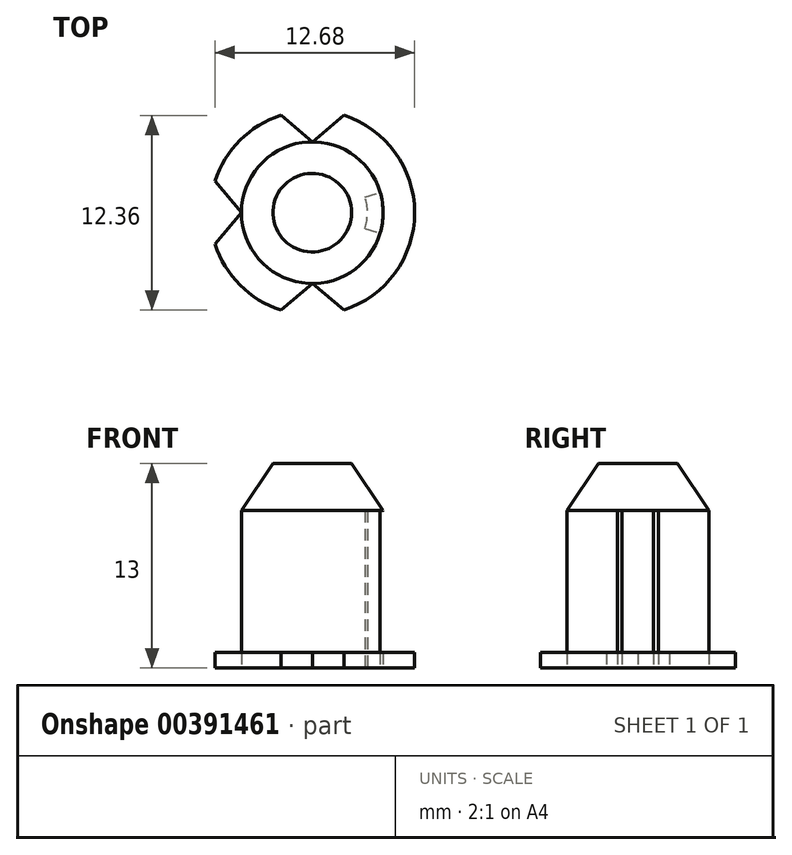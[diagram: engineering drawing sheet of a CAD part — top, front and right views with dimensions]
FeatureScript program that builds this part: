
annotation { "Feature Type Name" : "Feature", "Feature Type Description" : "" }
export const myFeature = defineFeature(function(context is Context, id is Id, definition is map)
    precondition{}
    {
        {
            var Q0;
            Q0=qCreatedBy(makeId("Top.planeOp"),FACE);
            var sketch = newSketch(context, id + "F0", { "sketchPlane" : qUnion([Q0])});
            skCircle(sketch, "E0", {"center": v(0, 0) * mm, "radius": 1.25 * mm});
            skCircle(sketch, "E1", {"center": v(0, 0) * mm, "radius": 6.5 * mm});
            skCircle(sketch, "E2.0", {"center": v(0, 0) * mm, "radius": 4.5 * mm});
            skArc(sketch, "E3", {"start": v(-6.18, 2) * mm, "mid": v(-6.5, 0) * mm, "end": v(-6.18, -2) * mm});
            skPoint(sketch, "E4.endSnap0", {"position": v(-6.5, 0) * mm});
            skCircle(sketch, "E5.0", {"center": v(0, 0) * mm, "radius": 3.5 * mm});
            skArc(sketch, "E6", {"start": v(3.35, -1) * mm, "mid": v(3.5, 0) * mm, "end": v(3.35, 1) * mm});
            skArc(sketch, "E7.0", {"start": v(4.3, -1.3) * mm, "mid": v(4.5, 0) * mm, "end": v(4.3, 1.3) * mm});
            skLineSegment(sketch, "E8", {"start": v(3.35, 1) * mm, "end": v(4.3, 1.3) * mm});
            skLineSegment(sketch, "E9", {"start": v(3.35, -1) * mm, "end": v(4.3, -1.3) * mm});
            skLineSegment(sketch, "E10", {"start": v(-6.18, 2) * mm, "end": v(-4.5, 0) * mm});
            skLineSegment(sketch, "E11", {"start": v(-4.5, 0) * mm, "end": v(-6.18, -2) * mm});
            skLineSegment(sketch, "E12", {"start": v(3.5, 0) * mm, "end": v(3.35, 1) * mm, "construction": true});
            skLineSegment(sketch, "E13", {"start": v(3.5, 0) * mm, "end": v(3.35, -1) * mm, "construction": true});
            skLineSegment(sketch, "E14", {"start": v(-4.5, 0) * mm, "end": v(-3.5, 0) * mm, "construction": true});
            skArc(sketch, "E15", {"start": v(-2, -6.18) * mm, "mid": v(0, -6.5) * mm, "end": v(2, -6.18) * mm});
            skLineSegment(sketch, "E16", {"start": v(-2, -6.18) * mm, "end": v(0, -4.5) * mm});
            skLineSegment(sketch, "E17", {"start": v(0, -4.5) * mm, "end": v(2, -6.18) * mm});
            skArc(sketch, "E18", {"start": v(2, 6.18) * mm, "mid": v(0, 6.5) * mm, "end": v(-2, 6.18) * mm});
            skLineSegment(sketch, "E19", {"start": v(2, 6.18) * mm, "end": v(0, 4.5) * mm});
            skLineSegment(sketch, "E20", {"start": v(0, 4.5) * mm, "end": v(-2, 6.18) * mm});
            skLineSegment(sketch, "E21", {"start": v(-3.5, 0) * mm, "end": v(-1.25, 0) * mm, "construction": true});
            skLineSegment(sketch, "E22", {"start": v(-1.25, 0) * mm, "end": v(1.25, 0) * mm, "construction": true});
            skLineSegment(sketch, "E23", {"start": v(1.25, 0) * mm, "end": v(3.5, 0) * mm, "construction": true});
            skLineSegment(sketch, "E24", {"start": v(3.35, -1) * mm, "end": v(1.2, -0.32) * mm, "construction": true});
            skLineSegment(sketch, "E25", {"start": v(3.35, 1) * mm, "end": v(1.2, 0.32) * mm, "construction": true});
            skCircle(sketch, "E26", {"center": v(0, 0) * mm, "radius": 2.5 * mm});
            skSolve(sketch);
        }
        {
            var Q0;
            {var subQ4=sQuery(id+"F0.wireOp",EDGE,"E10");Q0=makeQuery(id+"F0.imprint","IMPRINT",FACE,{"disambiguationData":[TD([[makeQuery(id+"F0.imprint","IMPRINT",EDGE,{"derivedFrom":subQ4}),1.0]])]});}
            var Q1;
            {var subQ0=sQuery(id+"F0.wireOp",EDGE,"E8");Q1=makeQuery(id+"F0.imprint","IMPRINT",FACE,{"disambiguationData":[TD([[makeQuery(id+"F0.imprint","IMPRINT",EDGE,{"derivedFrom":subQ0}),1.0]])]});}
            var Q2;
            {var subQ0=sQuery(id+"F0.wireOp",EDGE,"E11");Q2=makeQuery(id+"F0.imprint","IMPRINT",FACE,{"disambiguationData":[TD([[makeQuery(id+"F0.imprint","IMPRINT",EDGE,{"derivedFrom":subQ0}),1.0]])]});}
            var Q3;
            {var subQ2=sQuery(id+"F0.wireOp",EDGE,"E17");Q3=makeQuery(id+"F0.imprint","IMPRINT",FACE,{"disambiguationData":[TD([[makeQuery(id+"F0.imprint","IMPRINT",EDGE,{"derivedFrom":subQ2}),1.0]])]});}
            extrude(context, id + "F1", {"entities" : qUnion([Q0, Q1, Q2, Q3]), "depth" : 1 * mm});
        }
        {
            var Q0;
            {var subQ5=sQuery(id+"F0.wireOp",EDGE,"E8");Q0=makeQuery(id+"F0.imprint","IMPRINT",FACE,{"disambiguationData":[TD([[makeQuery(id+"F0.imprint","IMPRINT",EDGE,{"derivedFrom":subQ5}),1.0]])]});}
            var Q1;
            Q1=makeQuery(id+"F0.imprint","IMPRINT",FACE,{"disambiguationData":[TD([[makeQuery(id+"F0.imprint","IMPRINT",EDGE,{"derivedFrom":sQuery(id+"F0.wireOp",EDGE,"E26")}),-1.0]])]});
            var Q2;
            Q2=makeQuery(id+"F0.imprint","IMPRINT",FACE,{"disambiguationData":[TD([[makeQuery(id+"F0.imprint","IMPRINT",EDGE,{"derivedFrom":sQuery(id+"F0.wireOp",EDGE,"E0")}),-1.0]])]});
            var Q3;
            Q3=makeQuery(id+"F0.imprint","IMPRINT",FACE,{"disambiguationData":[TD([[makeQuery(id+"F0.imprint","IMPRINT",EDGE,{"derivedFrom":sQuery(id+"F0.wireOp",EDGE,"E0")}),1.0]])]});
            var Q4;
            {var subQ0=sQuery(id+"F0.wireOp",EDGE,"E8");Q4=makeQuery(id+"F0.imprint","IMPRINT",FACE,{"disambiguationData":[TD([[makeQuery(id+"F0.imprint","IMPRINT",EDGE,{"derivedFrom":subQ0}),-1.0]])]});}
            extrude(context, id + "F2", {"entities" : qUnion([Q0, Q1, Q2, Q3, Q4]), "operationType" : NewBodyOperationType.ADD, "depth" : 10 * mm});
        }
        {
            var Q0;
            Q0=makeQuery(id+"F1.opExtrude","SWEPT_BODY",BODY,{"disambiguationData":[OSD([sQuery(id+"F0.wireOp",EDGE,"E1"),sQuery(id+"F0.wireOp",EDGE,"E2.0"),sQuery(id+"F0.wireOp",EDGE,"E5.0"),sQuery(id+"F0.wireOp",EDGE,"E8"),sQuery(id+"F0.wireOp",EDGE,"E9"),sQuery(id+"F0.wireOp",EDGE,"E10"),sQuery(id+"F0.wireOp",EDGE,"E11"),sQuery(id+"F0.wireOp",EDGE,"E16"),sQuery(id+"F0.wireOp",EDGE,"E17"),sQuery(id+"F0.wireOp",EDGE,"E19"),sQuery(id+"F0.wireOp",EDGE,"E20")])]});
            transform(context, id + "F3", {"entities" : qUnion([Q0]), "transformType" : TransformType.TRANSLATION_3D, "dx" : 0 * mm, "dy" : 0 * mm, "dz" : -13 * mm, "makeCopy" : false});
        }
        {
            var Q0;
            Q0=makeQuery(id+"F0.imprint","IMPRINT",FACE,{"disambiguationData":[TD([[makeQuery(id+"F0.imprint","IMPRINT",EDGE,{"derivedFrom":sQuery(id+"F0.wireOp",EDGE,"E0")}),-1.0]])]});
            var Q1;
            Q1=makeQuery(id+"F0.imprint","IMPRINT",FACE,{"disambiguationData":[TD([[makeQuery(id+"F0.imprint","IMPRINT",EDGE,{"derivedFrom":sQuery(id+"F0.wireOp",EDGE,"E0")}),1.0]])]});
            extrude(context, id + "F4", {"entities" : qUnion([Q0, Q1]), "oppositeDirection" : true, "depth" : 1 * mm});
        }
        {
            var Q1;
            Q1=makeQuery(id+"F2.opExtrude","CAP_FACE",FACE,{"disambiguationData":[OSD([sQuery(id+"F0.wireOp",EDGE,"E2.0")])],"isStart":false});
            var Q2;
            Q2=makeQuery(id+"F4.opExtrude","CAP_FACE",FACE,{"disambiguationData":[OSD([sQuery(id+"F0.wireOp",EDGE,"E26")])],"isStart":true});
            loft(context, id + "F5", {"operationType" : NewBodyOperationType.ADD, "sheetProfilesArray" : [{ "sheetProfileEntities" : qUnion([Q1]) }, { "sheetProfileEntities" : qUnion([Q2]) }]});
        }
        {
            var Q0;
            Q0=makeQuery(id+"F0.imprint","IMPRINT",FACE,{"disambiguationData":[TD([[makeQuery(id+"F0.imprint","IMPRINT",EDGE,{"derivedFrom":sQuery(id+"F0.wireOp",EDGE,"E0")}),1.0]])]});
            var Q1;
            Q1=makeQuery(id+"F0.imprint","IMPRINT",FACE,{"disambiguationData":[TD([[makeQuery(id+"F0.imprint","IMPRINT",EDGE,{"derivedFrom":sQuery(id+"F0.wireOp",EDGE,"E0")}),-1.0]])]});
            var Q2;
            Q2=makeQuery(id+"F0.imprint","IMPRINT",FACE,{"disambiguationData":[TD([[makeQuery(id+"F0.imprint","IMPRINT",EDGE,{"derivedFrom":sQuery(id+"F0.wireOp",EDGE,"E26")}),-1.0]])]});
            extrude(context, id + "F6", {"entities" : qUnion([Q0, Q1, Q2]), "depth" : 10 * mm});
        }
        {
            var Q0;
            Q0=makeQuery(id+"F6.opExtrude","SWEPT_BODY",BODY,{"disambiguationData":[OSD([sQuery(id+"F0.wireOp",EDGE,"E5.0")])]});
            transform(context, id + "F7", {"entities" : qUnion([Q0]), "transformType" : TransformType.TRANSLATION_3D, "dx" : 0 * mm, "dy" : 0 * mm, "dz" : -13 * mm, "makeCopy" : false});
        }
        {
            var Q1;
            Q1=makeQuery(id+"F6.opExtrude","CAP_FACE",FACE,{"disambiguationData":[OSD([sQuery(id+"F0.wireOp",EDGE,"E5.0")])],"isStart":false});
            var Q2;
            Q2=makeQuery(id+"F0.imprint","IMPRINT",FACE,{"disambiguationData":[TD([[makeQuery(id+"F0.imprint","IMPRINT",EDGE,{"derivedFrom":sQuery(id+"F0.wireOp",EDGE,"E0")}),1.0]])]});
            loft(context, id + "F8", {"operationType" : NewBodyOperationType.ADD, "sheetProfilesArray" : [{ "sheetProfileEntities" : qUnion([Q1]) }, { "sheetProfileEntities" : qUnion([Q2]) }]});
        }
        {
            var Q0;
            {var subQ0=sQuery(id+"F0.wireOp",EDGE,"E8");Q0=makeQuery(id+"F0.imprint","IMPRINT",FACE,{"disambiguationData":[TD([[makeQuery(id+"F0.imprint","IMPRINT",EDGE,{"derivedFrom":subQ0}),-1.0]])]});}
            extrude(context, id + "F9", {"entities" : qUnion([Q0]), "depth" : 10 * mm});
        }
        {
            var Q0;
            Q0=makeQuery(id+"F9.opExtrude","SWEPT_BODY",BODY,{"disambiguationData":[OSD([sQuery(id+"F0.wireOp",EDGE,"E2.0"),sQuery(id+"F0.wireOp",EDGE,"E5.0"),sQuery(id+"F0.wireOp",EDGE,"E8"),sQuery(id+"F0.wireOp",EDGE,"E9")])]});
            transform(context, id + "F10", {"entities" : qUnion([Q0]), "transformType" : TransformType.TRANSLATION_3D, "dx" : 0 * mm, "dy" : 0 * mm, "dz" : -13 * mm, "makeCopy" : false});
        }
        {
            var Q0;
            Q0=makeQuery(id+"F6.opExtrude","SWEPT_BODY",BODY,{"disambiguationData":[OSD([sQuery(id+"F0.wireOp",EDGE,"E5.0")])]});
            var Q1;
            Q1=makeQuery(id+"F9.opExtrude","SWEPT_BODY",BODY,{"disambiguationData":[OSD([sQuery(id+"F0.wireOp",EDGE,"E2.0"),sQuery(id+"F0.wireOp",EDGE,"E5.0"),sQuery(id+"F0.wireOp",EDGE,"E8"),sQuery(id+"F0.wireOp",EDGE,"E9")])]});
            var Q2;
            Q2=makeQuery(id+"F1.opExtrude","SWEPT_BODY",BODY,{"disambiguationData":[OSD([sQuery(id+"F0.wireOp",EDGE,"E1"),sQuery(id+"F0.wireOp",EDGE,"E2.0"),sQuery(id+"F0.wireOp",EDGE,"E5.0"),sQuery(id+"F0.wireOp",EDGE,"E8"),sQuery(id+"F0.wireOp",EDGE,"E9"),sQuery(id+"F0.wireOp",EDGE,"E10"),sQuery(id+"F0.wireOp",EDGE,"E11"),sQuery(id+"F0.wireOp",EDGE,"E16"),sQuery(id+"F0.wireOp",EDGE,"E17"),sQuery(id+"F0.wireOp",EDGE,"E19"),sQuery(id+"F0.wireOp",EDGE,"E20")])]});
            booleanBodies(context, id + "F11", {"operationType" : BooleanOperationType.SUBTRACTION, "tools" : qUnion([Q0, Q1]), "targets" : qUnion([Q2])});
        }
    });
